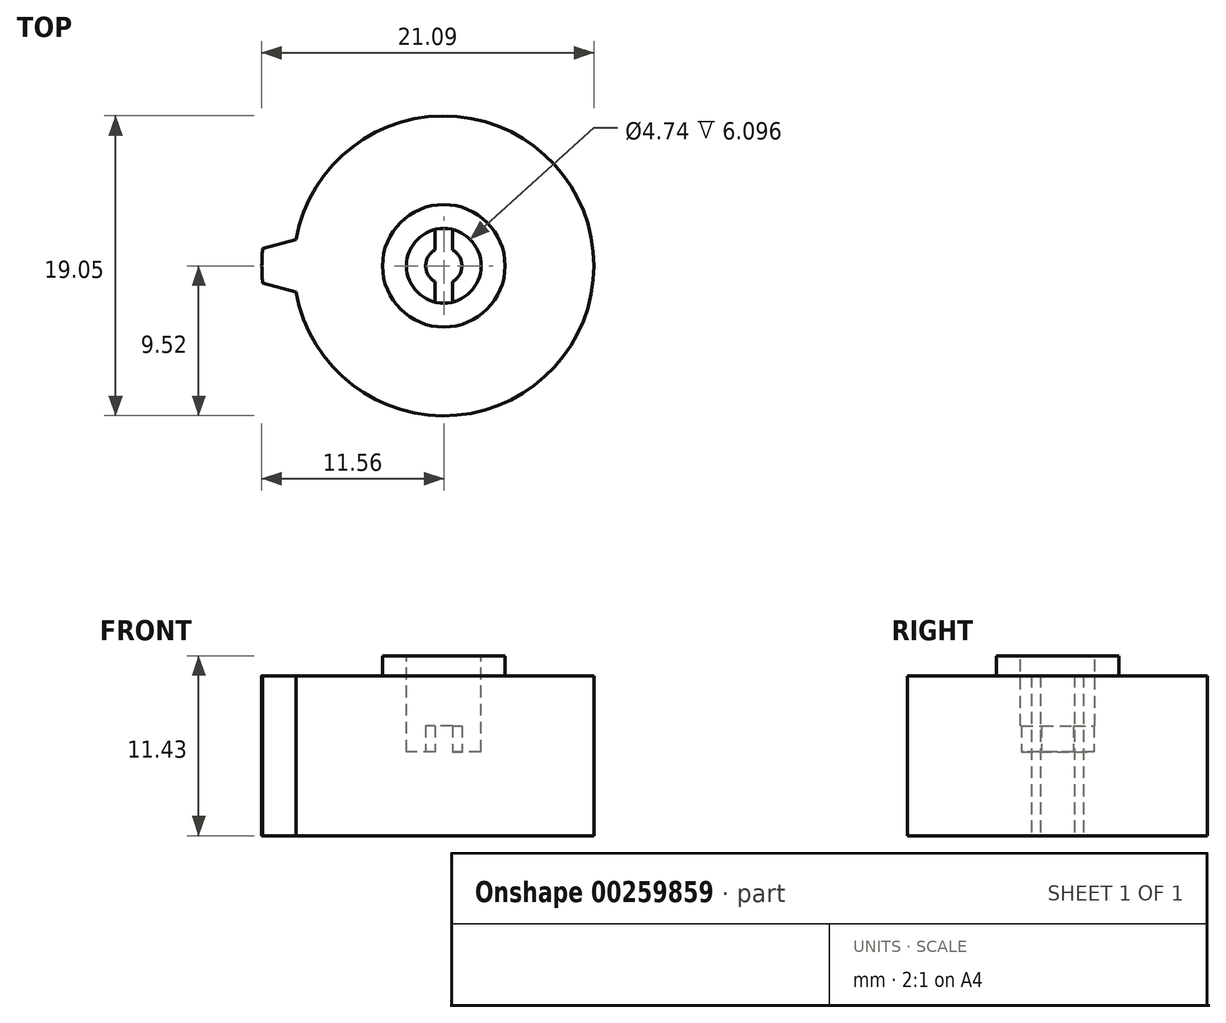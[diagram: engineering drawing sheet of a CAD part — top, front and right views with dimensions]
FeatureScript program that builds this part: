
annotation { "Feature Type Name" : "Feature", "Feature Type Description" : "" }
export const myFeature = defineFeature(function(context is Context, id is Id, definition is map)
    precondition{}
    {
        {
            assignVariable(context, id + "F0", {"name" : "Standoff", "anyValue" : 1.27 * mm});
        }
        {
            var Q0;
            Q0=qCreatedBy(makeId("Top.planeOp"),FACE);
            var sketch = newSketch(context, id + "F1", { "sketchPlane" : qUnion([Q0])});
            skArc(sketch, "E0", {"start": v(-9.38, -1.65) * mm, "mid": v(9.53, 0) * mm, "end": v(-9.38, 1.65) * mm});
            skArc(sketch, "E1", {"start": v(-11.5, 1.08) * mm, "mid": v(-11.56, 0) * mm, "end": v(-11.5, -1.08) * mm});
            skLineSegment(sketch, "E2", {"start": v(-11.5, 1.08) * mm, "end": v(-9.38, 1.65) * mm});
            skLineSegment(sketch, "E3", {"start": v(-11.5, -1.08) * mm, "end": v(-9.38, -1.65) * mm});
            skPoint(sketch, "E4", {"position": v(-11.56, 0) * mm});
            skLineSegment(sketch, "E5", {"start": v(-11.56, 0) * mm, "end": v(0, 0) * mm, "construction": true});
            skLineSegment(sketch, "E6", {"start": v(-9.38, 1.65) * mm, "end": v(0, 0) * mm, "construction": true});
            skLineSegment(sketch, "E7", {"start": v(-9.38, -1.65) * mm, "end": v(0, 0) * mm, "construction": true});
            skArc(sketch, "E8", {"start": v(-9.38, 1.65) * mm, "mid": v(-9.52, 0) * mm, "end": v(-9.38, -1.65) * mm, "construction": true});
            skPoint(sketch, "E9", {"position": v(-9.53, 0) * mm});
            skSolve(sketch);
        }
        {
            var Q0;
            Q0 = qSketchRegion(id + "F1", true);
            extrude(context, id + "F2", {"entities" : qUnion([Q0]), "depth" : 10.16 * mm});
        }
        {
            var Q0;
            Q0=makeQuery(id+"F2.opExtrude","CAP_FACE",FACE,{"disambiguationData":[OSD([sQuery(id+"F1.wireOp",EDGE,"E0"),sQuery(id+"F1.wireOp",EDGE,"E1"),sQuery(id+"F1.wireOp",EDGE,"E2"),sQuery(id+"F1.wireOp",EDGE,"E3")])],"isStart":false});
            var sketch = newSketch(context, id + "F3", { "sketchPlane" : qUnion([Q0])});
            skCircle(sketch, "E10", {"center": v(0, 0) * mm, "radius": 3.9 * mm});
            skCircle(sketch, "E11", {"center": v(0, 0) * mm, "radius": 2.37 * mm, "construction": true});
            skSolve(sketch);
        }
        {
            var Q0;
            Q0 = qSketchRegion(id + "F3", true);
            extrude(context, id + "F4", {"entities" : qUnion([Q0]), "operationType" : NewBodyOperationType.ADD, "depth" : getVariable(context, 'Standoff')});
        }
        {
            var Q0;
            Q0=makeQuery(id+"F4.opExtrude","CAP_FACE",FACE,{"disambiguationData":[OSD([sQuery(id+"F3.wireOp",EDGE,"E10")])],"isStart":false});
            var sketch = newSketch(context, id + "F5", { "sketchPlane" : qUnion([Q0])});
            skCircle(sketch, "E12", {"center": v(0, 0) * mm, "radius": 2.37 * mm});
            skSolve(sketch);
        }
        {
            var Q0;
            Q0 = qSketchRegion(id + "F5", true);
            extrude(context, id + "F6", {"entities" : qUnion([Q0]), "operationType" : NewBodyOperationType.REMOVE, "oppositeDirection" : true, "depth" : 6.1 * mm});
        }
        {
            var Q0;
            Q0=makeQuery(id+"F6.boolean.opBoolean","COPY",FACE,{"derivedFrom":makeQuery(id+"F6.opExtrude","CAP_FACE",FACE,{"disambiguationData":[OSD([sQuery(id+"F5.wireOp",EDGE,"E12")])],"isStart":false})});
            var sketch = newSketch(context, id + "F7", { "sketchPlane" : qUnion([Q0])});
            skArc(sketch, "E13", {"start": v(-0.55, 2.3) * mm, "mid": v(0, 2.37) * mm, "end": v(0.55, 2.3) * mm});
            skArc(sketch, "E14", {"start": v(-0.55, -2.3) * mm, "mid": v(0, -2.37) * mm, "end": v(0.55, -2.3) * mm});
            skArc(sketch, "E15", {"start": v(0.55, -1) * mm, "mid": v(1.15, 0) * mm, "end": v(0.55, 1) * mm});
            skArc(sketch, "E16", {"start": v(-0.55, -1) * mm, "mid": v(-1.15, 0) * mm, "end": v(-0.55, 1) * mm});
            skLineSegment(sketch, "E17", {"start": v(-0.55, -1) * mm, "end": v(-0.55, -2.3) * mm});
            skLineSegment(sketch, "E18", {"start": v(0.55, -2.3) * mm, "end": v(0.55, -1) * mm});
            skLineSegment(sketch, "E19", {"start": v(0.55, 1) * mm, "end": v(0.55, 2.3) * mm});
            skLineSegment(sketch, "E20", {"start": v(-0.55, 2.3) * mm, "end": v(-0.55, 1) * mm});
            skPoint(sketch, "E21", {"position": v(0, 2.37) * mm});
            skPoint(sketch, "E22", {"position": v(0, -2.37) * mm});
            skSolve(sketch);
        }
        {
            var Q0;
            Q0 = qSketchRegion(id + "F7", true);
            extrude(context, id + "F8", {"entities" : qUnion([Q0]), "operationType" : NewBodyOperationType.ADD, "depth" : 1.65 * mm});
        }
    });
